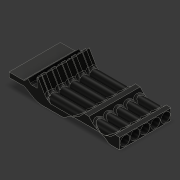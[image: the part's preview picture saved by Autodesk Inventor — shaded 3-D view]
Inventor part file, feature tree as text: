
AUTODESK INVENTOR PART (.ipt)
format: ipt  version: 2020.2 (Build 242310000, 310)  size: 1,229,312 bytes
history: native  units: mm
features: other x14, extrude x8, fillet x6, loft x2, chamfer x2, sketch x2, pattern_linear x1, projected_geometry x1
ambient origin geometry x8: Origin, YZ Plane, XZ Plane, XY Plane, X Axis, Y Axis, Z Axis, Center Point
bodies: Solid1 (feature_tree)
feature tree (36):
  other  "CrossSection1"
  other  "Block Sketch"
  extrude  "Block"  Depth=7.0mm
  extrude  "Hinge Indexer"  Depth=20.0mm
  fillet  "Hinge Indexer Fillet"  Radius=9.525mm
  extrude  "Duct"  Depth=6.35mm
  other  "Valve Fitting"
  loft  "Fitting to Duct"
  other  "Mouth End Plane"
  other  "Loose Socket Start Plane"
  other  "Edge Loft Start Plane"
  other  "Pipe Socket Sketch"
  extrude  "Pipe Socket (Tight)"  Depth=20.0mm
  extrude  "Punch through to pipe"  Depth=20.0mm
  extrude  "Pipe Socket (Loose)"  Depth=1.0mm
  extrude  "Mouth Cavity"  Depth=1.0mm
  loft  "Loft2"
  fillet  "Fillet2"  [1 undecoded]
  fillet  "Fillet3"  Radius=13.0625mm
  extrude  "Pipe Holder Cut"  Depth=20.0mm
  fillet  "Fillet7"  Radius=17.03125mm
  chamfer  "Chamfer1"  Distance=6.5mm
  chamfer  "Chamfer2"  Distance=10.0mm
  fillet  "Fillet9"  Radius=1.0mm
  pattern_linear  "Key Repetition"  Spacing1=999.0mm  [1 undecoded]
  fillet  "Fillet11"  Radius=6.35mm
  other  "Mouth Start Plane"
  other  "Duct Sketch"
  other  "Valve Fitting Sketch"
  other  "Tight Socket Start Plane"
  sketch  "Sketch5"  dims[d2=0.5mm d3=7.0mm]
  projected_geometry  "Projected Loop1"
  other  "Edges1"
  sketch  "Sketch6"  dims[d9=0.0mm d13=4.7625mm d14=9.525mm d15=6.35mm d18=0.25mm d19=5.0mm d21=3.0mm d24=1.0mm d26=1.0mm d27=1.0mm d36=90.0deg d39=13.0625mm d40=3.0mm d41=17.03125mm d43=6.5mm d46=10.0mm d49=1.0mm d50=999.0mm d51=0.0mm d52=999.0mm d53=0.0mm d54=6.35mm d55=0.0mm d56=0.5mm d57=2.0mm d58=-4.75mm d59=20.0mm d60=0.0mm d61=90.0deg d62=0.0mm d63=90.0deg d64=10.0mm d65=0.0mm d68=10.0mm d69=63.858mm d70=0.0mm d71=1.5mm d72=4.11mm d73=0.0mm d74=0.5mm d75=135.0deg d76=135.0deg d77=135.0deg d78=5.7625mm d79=2.88125mm d84=50.0mm d86=10.775mm d87=-5.0mm d88=0.0mm d89=90.0deg d90=0.0mm d91=90.0deg d93=30.0mm d95=8.26mm d96=0.0mm d98=5.7625mm d104=0.75mm d113=5.7625mm d118=60.0deg d119=20.20625mm d124=1.5875mm d125=2.0mm d126=30.0deg d128=0.25mm d129=2.0mm d130=30.0deg d131=17.03125mm d133=3.5875mm d134=55.0mm d135=88.0mm d139=45.0deg d147=5.0mm d148=10.0mm d153=20.0mm d154=4.0mm]
  other  "Edges2"
  other  "Pipe Holder Cut Sketch"
note: 2 required parameter values undecoded (feature->parameter linkage not recoverable at this tier; creation-order binding heuristic only, values carry confidence <= 0.55)
